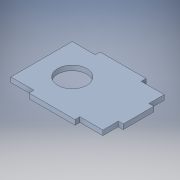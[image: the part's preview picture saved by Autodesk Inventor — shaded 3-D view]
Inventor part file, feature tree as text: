
AUTODESK INVENTOR PART (.ipt)
format: ipt  version: 2019 (Build 230136000, 136)  size: 130,048 bytes
history: native  units: mm
features: other x1, extrude x1, sketch x1
ambient origin geometry x8: Origin, YZ Plane, XZ Plane, XY Plane, X Axis, Y Axis, Z Axis, Center Point
bodies: Body1 (feature_tree)
feature tree (3):
  other  "Sólido1"
  extrude  "Extrusión1"  Depth=3.18mm TaperAngle=0.0deg
  sketch  "Boceto1"  dims[d0=19.0mm d17=40.0mm d18=60.0mm d19=20.0mm d20=20.0mm d21=3.18mm d22=30.0mm d23=15.0mm d24=20.0mm d25=10.0mm d26=3.18mm d27=3.18mm d28=0.0mm]
